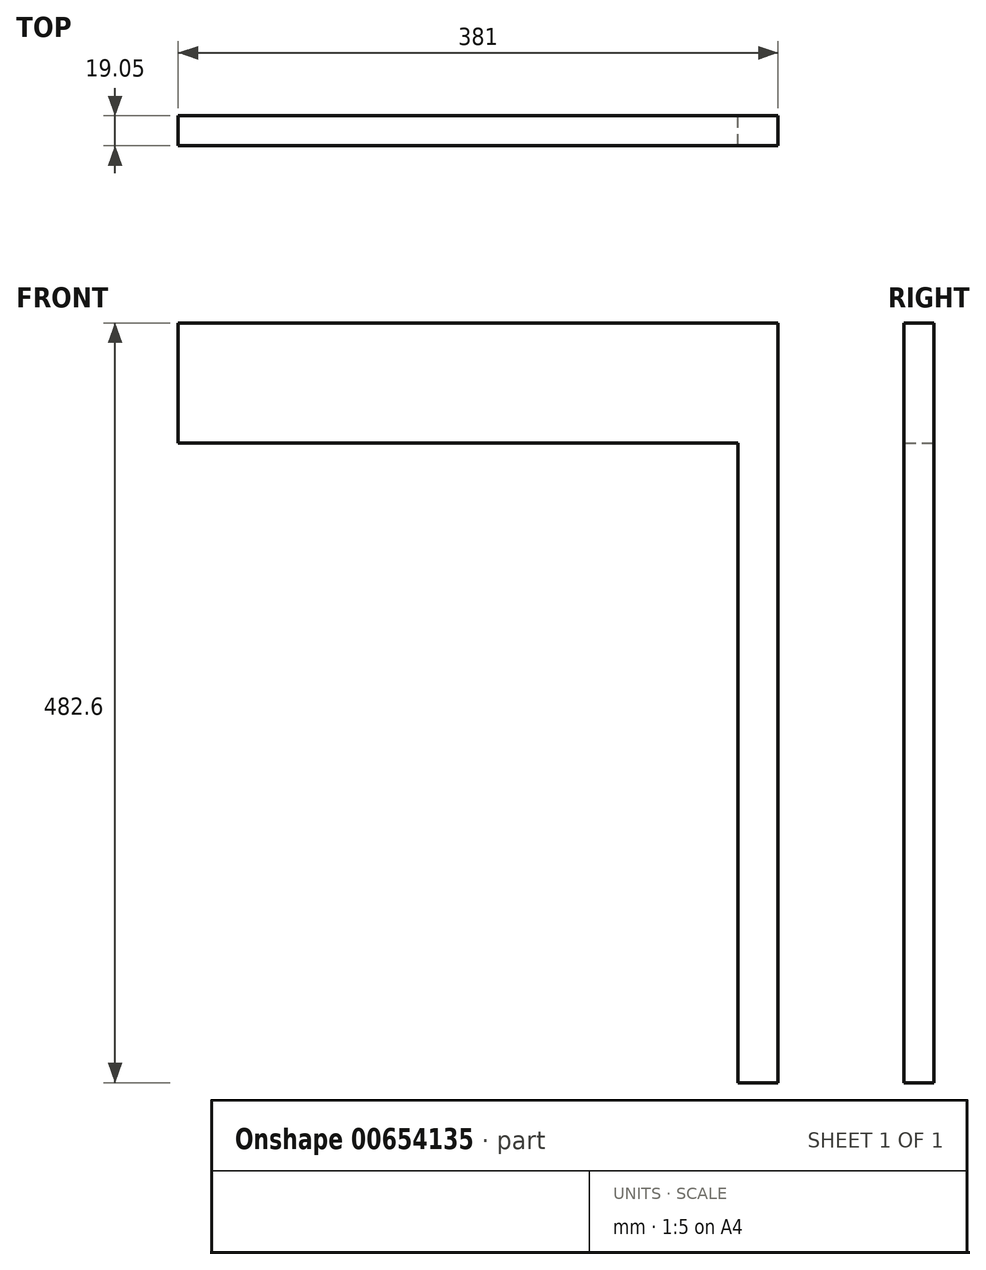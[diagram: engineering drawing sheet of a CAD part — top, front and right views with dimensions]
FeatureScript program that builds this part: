
annotation { "Feature Type Name" : "Feature", "Feature Type Description" : "" }
export const myFeature = defineFeature(function(context is Context, id is Id, definition is map)
    precondition{}
    {
        {
            var Q0;
            Q0=qCreatedBy(makeId("Front.planeOp"),FACE);
            var sketch = newSketch(context, id + "F0", { "sketchPlane" : qUnion([Q0])});
            skLineSegment(sketch, "E0.bottom", {"start": v(-185.45, 38.1) * mm, "end": v(195.55, 38.1) * mm});
            skLineSegment(sketch, "E0.left", {"start": v(-185.45, 38.1) * mm, "end": v(-185.45, -38.1) * mm});
            skLineSegment(sketch, "E0.right", {"start": v(195.55, 38.1) * mm, "end": v(195.55, -38.1) * mm});
            skPoint(sketch, "E0.middle", {"position": v(5.05, 0) * mm});
            skLineSegment(sketch, "E1", {"start": v(-185.45, -38.1) * mm, "end": v(170.15, -38.1) * mm});
            skLineSegment(sketch, "E2", {"start": v(170.15, -38.1) * mm, "end": v(170.15, -444.5) * mm});
            skLineSegment(sketch, "E3", {"start": v(170.15, -444.5) * mm, "end": v(195.55, -444.5) * mm});
            skLineSegment(sketch, "E4", {"start": v(195.55, -444.5) * mm, "end": v(195.55, -38.1) * mm});
            skSolve(sketch);
        }
        {
            var Q0;
            Q0=qSketchRegion(id+"F0",true);
            extrude(context, id + "F1", {"entities" : qUnion([Q0]), "depth" : 19.05 * mm, "offsetDistance" : 25.4 * mm});
        }
    });
